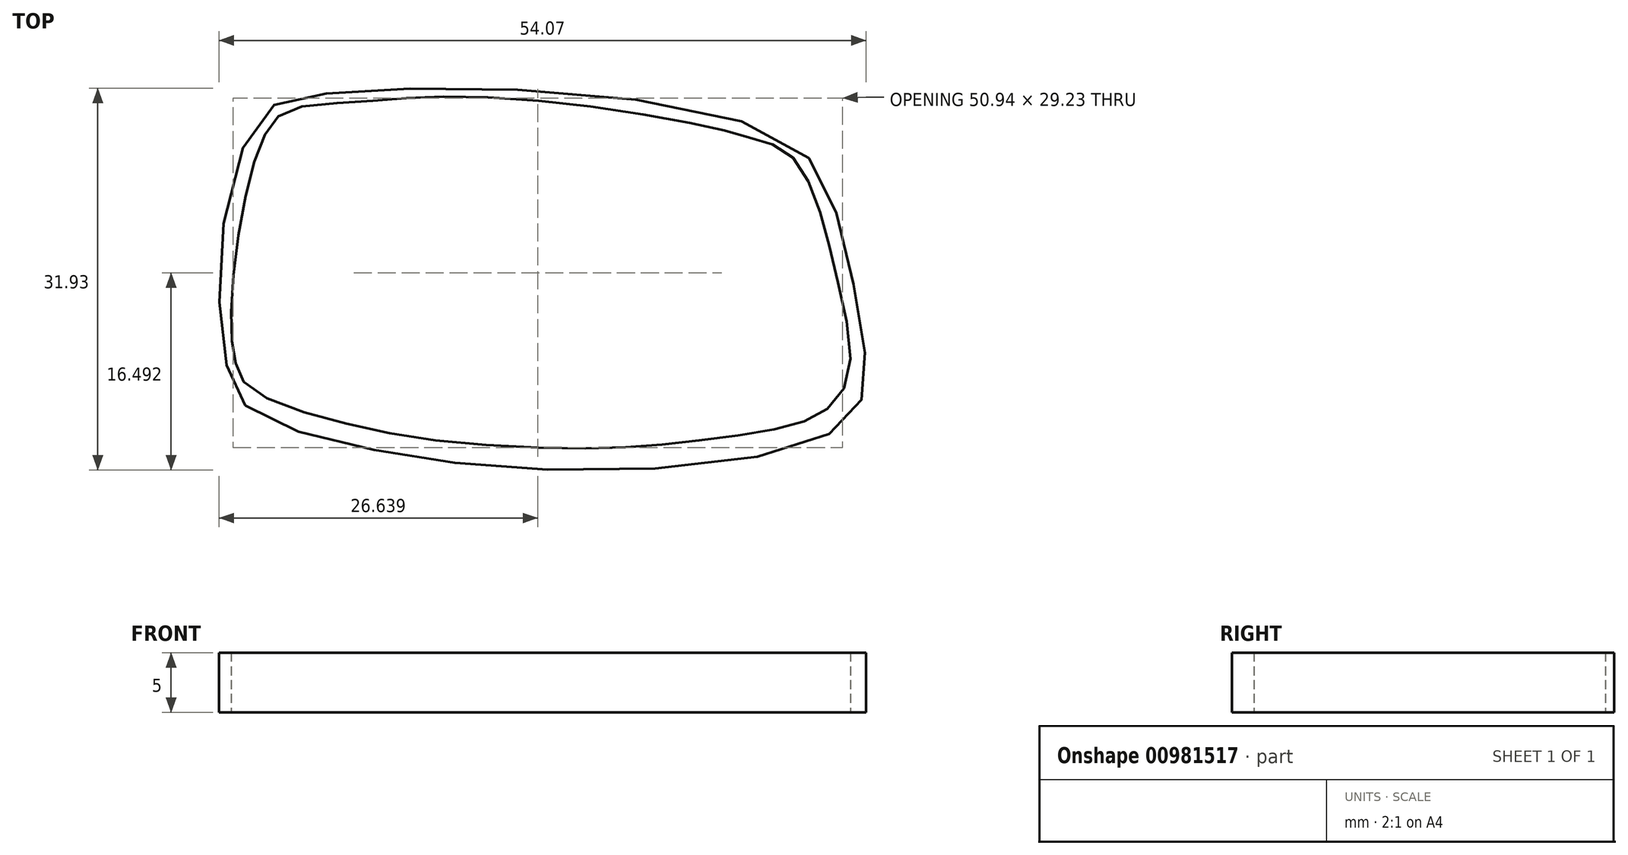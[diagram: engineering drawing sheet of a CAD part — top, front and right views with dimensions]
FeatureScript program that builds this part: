
annotation { "Feature Type Name" : "Feature", "Feature Type Description" : "" }
export const myFeature = defineFeature(function(context is Context, id is Id, definition is map)
    precondition{}
    {
        {
            var Q0;
            Q0=qCreatedBy(makeId("Top.planeOp"),FACE);
            var sketch = newSketch(context, id + "F0", { "sketchPlane" : qUnion([Q0])});
            skFitSpline(sketch, "E0", {"points": [v(37.55, -40.36) * mm, v(37.07, -30.36) * mm, v(40.25, -19.72) * mm, v(44.38, -17.82) * mm, v(62, -17.34) * mm, v(84.7, -21.79) * mm, v(88.82, -28.77) * mm, v(90.88, -39.25) * mm, v(90.4, -43.7) * mm, v(85.33, -47.18) * mm, v(64.22, -49.09) * mm, v(48.66, -47.18) * mm, v(39.46, -44) * mm, v(37.55, -40.36) * mm]});
            skFitSpline(sketch, "E1", {"points": [v(38.35, -40.35) * mm, v(37.96, -37.87) * mm, v(38.22, -32) * mm, v(39.53, -24.55) * mm, v(41.03, -20.56) * mm, v(42.86, -19) * mm, v(48.6, -18.34) * mm, v(54.35, -17.95) * mm, v(65.2, -18.4) * mm, v(77.86, -20.43) * mm, v(81.78, -21.48) * mm, v(84.6, -22.73) * mm, v(86.87, -26.72) * mm, v(88.65, -33.4) * mm, v(89.6, -40.9) * mm, v(87.56, -44.17) * mm, v(83.4, -45.7) * mm, v(75.77, -46.79) * mm, v(68.2, -47.3) * mm, v(55.76, -46.71) * mm, v(45.93, -44.82) * mm, v(39.46, -42.2) * mm, v(38.35, -40.35) * mm]});
            skLineSegment(sketch, "E2", {"start": v(63.6, -47.25) * mm, "end": v(63.6, -18.25) * mm});
            skSolve(sketch);
        }
        {
            var Q0;
            Q0 = qSketchRegion(id + "F0", true);
            extrude(context, id + "F1", {"entities" : qUnion([Q0]), "depth" : 5 * mm, "offsetDistance" : 25.4 * mm});
        }
    });
